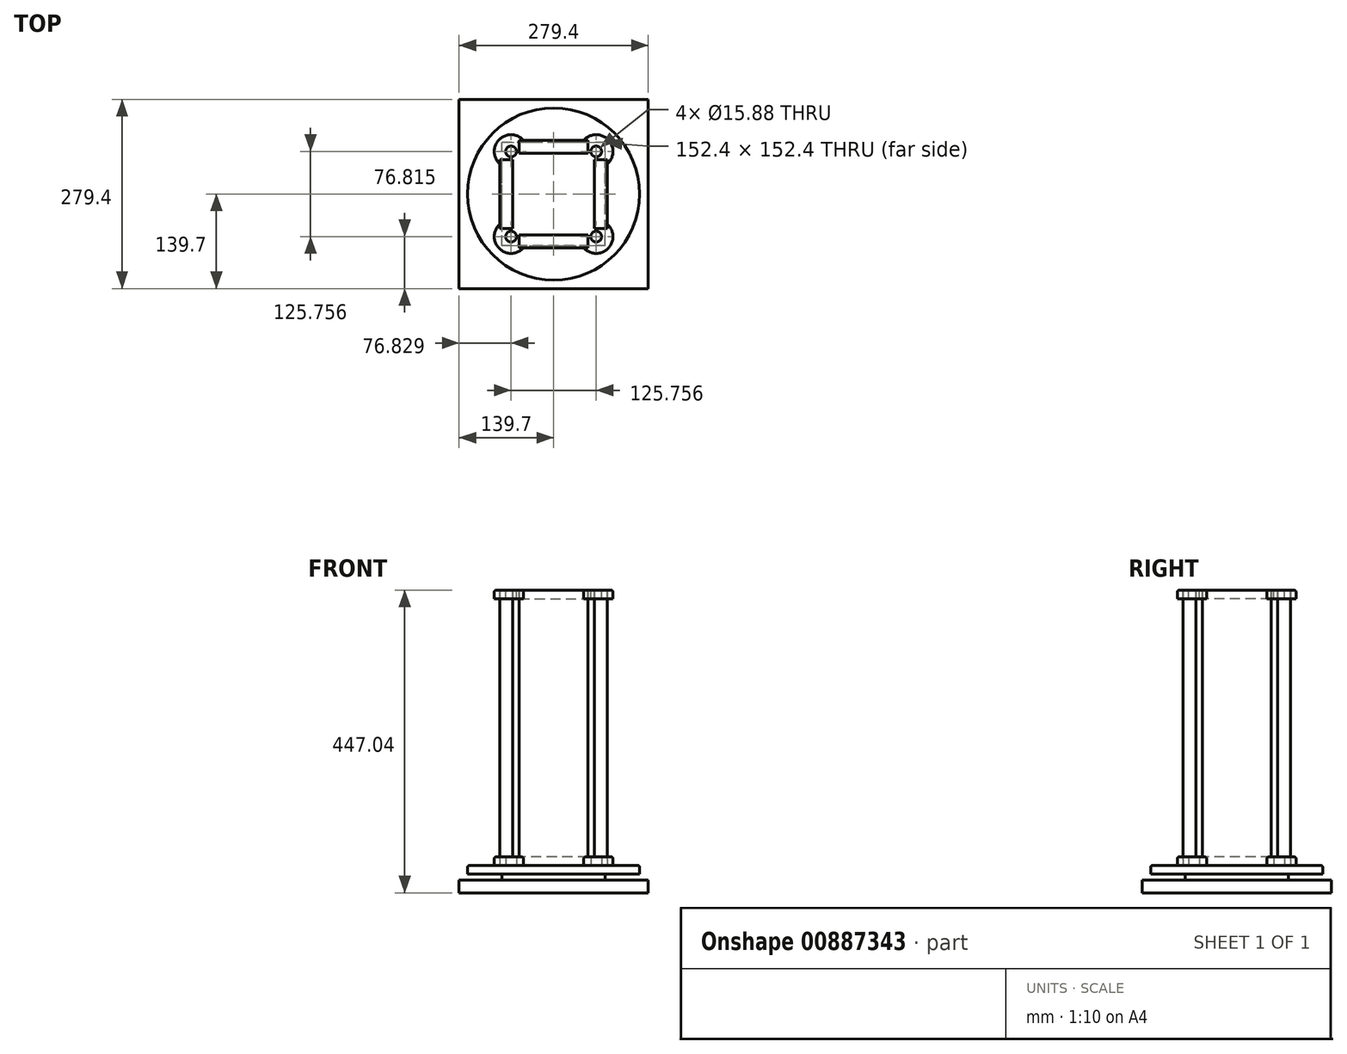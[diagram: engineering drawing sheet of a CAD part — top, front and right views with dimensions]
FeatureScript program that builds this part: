
annotation { "Feature Type Name" : "Feature", "Feature Type Description" : "" }
export const myFeature = defineFeature(function(context is Context, id is Id, definition is map)
    precondition{}
    {
        {
            var Q0;
            Q0=qCreatedBy(makeId("Top.planeOp"),FACE);
            var sketch = newSketch(context, id + "F0", { "sketchPlane" : qUnion([Q0])});
            skLineSegment(sketch, "E0.bottom", {"start": v(-139.7, 139.7) * mm, "end": v(139.7, 139.7) * mm});
            skLineSegment(sketch, "E0.top", {"start": v(-139.7, -139.7) * mm, "end": v(139.7, -139.7) * mm});
            skLineSegment(sketch, "E0.left", {"start": v(-139.7, 139.7) * mm, "end": v(-139.7, -139.7) * mm});
            skLineSegment(sketch, "E0.right", {"start": v(139.7, 139.7) * mm, "end": v(139.7, -139.7) * mm});
            skPoint(sketch, "E0.middle", {"position": v(0, 0) * mm});
            skSolve(sketch);
        }
        {
            var Q0;
            Q0=makeQuery(id+"F0.imprint","IMPRINT",FACE,{"disambiguationData":[TD([[makeQuery(id+"F0.imprint","IMPRINT",EDGE,{"derivedFrom":sQuery(id+"F0.wireOp",EDGE,"E0.bottom")}),-1.0]])]});
            extrude(context, id + "F1", {"entities" : qUnion([Q0]), "depth" : 19.05 * mm, "offsetDistance" : 25.4 * mm});
        }
        {
            var Q0;
            Q0=makeQuery(id+"F1.opExtrude","CAP_FACE",FACE,{"disambiguationData":[OSD([sQuery(id+"F0.wireOp",EDGE,"E0.bottom"),sQuery(id+"F0.wireOp",EDGE,"E0.top"),sQuery(id+"F0.wireOp",EDGE,"E0.left"),sQuery(id+"F0.wireOp",EDGE,"E0.right")])],"isStart":false});
            var sketch = newSketch(context, id + "F2", { "sketchPlane" : qUnion([Q0])});
            skLineSegment(sketch, "E1.bottom", {"start": v(76.2, -76.2) * mm, "end": v(-76.2, -76.2) * mm});
            skLineSegment(sketch, "E1.top", {"start": v(76.2, 76.2) * mm, "end": v(-76.2, 76.2) * mm});
            skLineSegment(sketch, "E1.left", {"start": v(76.2, -76.2) * mm, "end": v(76.2, 76.2) * mm});
            skLineSegment(sketch, "E1.right", {"start": v(-76.2, -76.2) * mm, "end": v(-76.2, 76.2) * mm});
            skPoint(sketch, "E1.middle", {"position": v(0, 0) * mm});
            skSolve(sketch);
        }
        {
            var Q0;
            Q0 = qSketchRegion(id + "F2", true);
            extrude(context, id + "F3", {"entities" : qUnion([Q0]), "operationType" : NewBodyOperationType.ADD, "depth" : 8.9 * mm, "offsetDistance" : 25.4 * mm});
        }
        {
            var Q0;
            Q0=qCreatedBy(makeId("Top.planeOp"),FACE);
            cPlane(context, id + "F4", {"entities" : qUnion([Q0]), "cplaneType" : CPlaneType.OFFSET, "offset" : 27.94 * mm, "width" : 152.4 * mm, "height" : 152.4 * mm});
        }
        {
            var Q0;
            Q0=qCreatedBy(id+"F4.planeOp",FACE);
            var sketch = newSketch(context, id + "F5", { "sketchPlane" : qUnion([Q0])});
            skCircle(sketch, "E2", {"center": v(0, 0) * mm, "radius": 127 * mm});
            skSolve(sketch);
        }
        {
            var Q0;
            Q0=makeQuery(id+"F5.imprint","IMPRINT",FACE,{"disambiguationData":[TD([[makeQuery(id+"F5.imprint","IMPRINT",EDGE,{"derivedFrom":sQuery(id+"F5.wireOp",EDGE,"E2")}),1.0]])]});
            extrude(context, id + "F6", {"entities" : qUnion([Q0]), "operationType" : NewBodyOperationType.ADD, "depth" : 12.7 * mm, "offsetDistance" : 25.4 * mm});
        }
        {
            var Q0;
            Q0=makeQuery(id+"F6.opExtrude","CAP_FACE",FACE,{"disambiguationData":[OSD([sQuery(id+"F5.wireOp",EDGE,"E2")])],"isStart":false});
            var sketch = newSketch(context, id + "F7", { "sketchPlane" : qUnion([Q0])});
            skLineSegment(sketch, "E3.bottom", {"start": v(50.8, -79.38) * mm, "end": v(-50.8, -79.38) * mm});
            skLineSegment(sketch, "E3.top", {"start": v(50.8, -60.33) * mm, "end": v(-50.8, -60.32) * mm});
            skLineSegment(sketch, "E3.left", {"start": v(50.8, -79.38) * mm, "end": v(50.8, -60.33) * mm});
            skLineSegment(sketch, "E3.right", {"start": v(-50.8, -79.38) * mm, "end": v(-50.8, -60.32) * mm});
            skPoint(sketch, "E3.middle", {"position": v(0, -69.85) * mm});
            skLineSegment(sketch, "E4.1.0", {"start": v(79.38, 50.8) * mm, "end": v(79.38, -50.8) * mm});
            skLineSegment(sketch, "E4.1.1", {"start": v(79.38, -50.8) * mm, "end": v(60.32, -50.8) * mm});
            skLineSegment(sketch, "E4.1.2", {"start": v(60.33, 50.8) * mm, "end": v(60.32, -50.8) * mm});
            skLineSegment(sketch, "E4.1.3", {"start": v(79.38, 50.8) * mm, "end": v(60.33, 50.8) * mm});
            skLineSegment(sketch, "E4.2.0", {"start": v(-50.8, 79.38) * mm, "end": v(50.8, 79.38) * mm});
            skLineSegment(sketch, "E4.2.1", {"start": v(50.8, 79.38) * mm, "end": v(50.8, 60.32) * mm});
            skLineSegment(sketch, "E4.2.2", {"start": v(-50.8, 60.33) * mm, "end": v(50.8, 60.32) * mm});
            skLineSegment(sketch, "E4.2.3", {"start": v(-50.8, 79.38) * mm, "end": v(-50.8, 60.33) * mm});
            skLineSegment(sketch, "E4.3.0", {"start": v(-79.38, -50.8) * mm, "end": v(-79.38, 50.8) * mm});
            skLineSegment(sketch, "E4.3.1", {"start": v(-79.38, 50.8) * mm, "end": v(-60.32, 50.8) * mm});
            skLineSegment(sketch, "E4.3.2", {"start": v(-60.33, -50.8) * mm, "end": v(-60.32, 50.8) * mm});
            skLineSegment(sketch, "E4.3.3", {"start": v(-79.38, -50.8) * mm, "end": v(-60.33, -50.8) * mm});
            skPoint(sketch, "E4.center", {"position": v(0, 0) * mm});
            skCircle(sketch, "E5", {"center": v(-62.87, -62.86) * mm, "radius": 7.94 * mm});
            skLineSegment(sketch, "E6", {"start": v(-62.87, -62.86) * mm, "end": v(0, 0) * mm, "construction": true});
            skLineSegment(sketch, "E7", {"start": v(0, 0) * mm, "end": v(0, -69.85) * mm, "construction": true});
            skLineSegment(sketch, "E8", {"start": v(-62.87, -62.86) * mm, "end": v(-50.8, -62.86) * mm, "construction": true});
            skLineSegment(sketch, "E9", {"start": v(-62.87, -62.86) * mm, "end": v(-62.87, -50.8) * mm, "construction": true});
            skCircle(sketch, "E10.1.0", {"center": v(62.86, -62.87) * mm, "radius": 7.94 * mm});
            skCircle(sketch, "E10.2.0", {"center": v(62.87, 62.86) * mm, "radius": 7.94 * mm});
            skCircle(sketch, "E10.3.0", {"center": v(-62.86, 62.87) * mm, "radius": 7.94 * mm});
            skSolve(sketch);
        }
        {
            var Q0;
            Q0=makeQuery(id+"F7.imprint","IMPRINT",FACE,{"disambiguationData":[TD([[makeQuery(id+"F7.imprint","IMPRINT",EDGE,{"derivedFrom":sQuery(id+"F7.wireOp",EDGE,"E3.bottom")}),-1.0]])]});
            var Q1;
            Q1=makeQuery(id+"F7.imprint","IMPRINT",FACE,{"disambiguationData":[TD([[makeQuery(id+"F7.imprint","IMPRINT",EDGE,{"derivedFrom":sQuery(id+"F7.wireOp",EDGE,"E4.3.0")}),-1.0]])]});
            var Q2;
            Q2=makeQuery(id+"F7.imprint","IMPRINT",FACE,{"disambiguationData":[TD([[makeQuery(id+"F7.imprint","IMPRINT",EDGE,{"derivedFrom":sQuery(id+"F7.wireOp",EDGE,"E4.2.0")}),-1.0]])]});
            var Q3;
            Q3=makeQuery(id+"F7.imprint","IMPRINT",FACE,{"disambiguationData":[TD([[makeQuery(id+"F7.imprint","IMPRINT",EDGE,{"derivedFrom":sQuery(id+"F7.wireOp",EDGE,"E4.1.0")}),-1.0]])]});
            extrude(context, id + "F8", {"entities" : qUnion([Q0, Q1, Q2, Q3]), "operationType" : NewBodyOperationType.ADD, "depth" : 406.4 * mm, "offsetDistance" : 25.4 * mm});
        }
        {
            var Q0;
            Q0=sQuery(id+"F7.wireOp",EDGE,"E10.3.0");
            var Q1;
            Q1=sQuery(id+"F7.wireOp",EDGE,"E10.2.0");
            var Q2;
            Q2=sQuery(id+"F7.wireOp",EDGE,"E10.1.0");
            var Q3;
            Q3=sQuery(id+"F7.wireOp",EDGE,"E5");
            extrude(context, id + "F9", {"bodyType" : ToolBodyType.SURFACE, "surfaceEntities" : qUnion([Q0, Q1, Q2, Q3]), "depth" : 406.4 * mm, "offsetDistance" : 25.4 * mm});
        }
        {
            var Q0;
            Q0=qCreatedBy(makeId("Front.planeOp"),FACE);
            cPlane(context, id + "F10", {"entities" : qUnion([Q0]), "cplaneType" : CPlaneType.OFFSET, "offset" : 50.8 * mm, "width" : 152.4 * mm, "height" : 152.4 * mm});
        }
        {
            var Q0;
            Q0=qCreatedBy(id+"F10.planeOp",FACE);
            var sketch = newSketch(context, id + "F11", { "sketchPlane" : qUnion([Q0])});
            skLineSegment(sketch, "E11", {"start": v(0, 0) * mm, "end": v(-62.87, 0) * mm, "construction": true});
            skLineSegment(sketch, "E12", {"start": v(-62.87, 0) * mm, "end": v(-62.87, 457.2) * mm, "construction": true});
            skLineSegment(sketch, "E13", {"start": v(0, 0) * mm, "end": v(0, 518.12) * mm, "construction": true});
            skCircle(sketch, "E14", {"center": v(-62.87, 457.2) * mm, "radius": 7.94 * mm});
            skCircle(sketch, "E15.MirrorC", {"center": v(62.87, 457.2) * mm, "radius": 7.94 * mm});
            skSolve(sketch);
        }
        {
            var Q0;
            Q0=sQuery(id+"F11.wireOp",EDGE,"E14");
            var Q1;
            Q1=sQuery(id+"F11.wireOp",EDGE,"E15.MirrorC");
            extrude(context, id + "F12", {"bodyType" : ToolBodyType.SURFACE, "surfaceEntities" : qUnion([Q0, Q1]), "oppositeDirection" : true, "depth" : 101.6 * mm, "offsetDistance" : 25.4 * mm});
        }
        {
            var Q0;
            Q0=qCreatedBy(makeId("Right.planeOp"),FACE);
            cPlane(context, id + "F13", {"entities" : qUnion([Q0]), "cplaneType" : CPlaneType.OFFSET, "offset" : 50.8 * mm, "width" : 152.4 * mm, "height" : 152.4 * mm});
        }
        {
            var Q0;
            Q0=qCreatedBy(id+"F13.planeOp",FACE);
            var sketch = newSketch(context, id + "F14", { "sketchPlane" : qUnion([Q0])});
            skLineSegment(sketch, "E16", {"start": v(0, 0) * mm, "end": v(62.87, 0) * mm, "construction": true});
            skLineSegment(sketch, "E17", {"start": v(62.87, 0) * mm, "end": v(62.87, 457.2) * mm, "construction": true});
            skLineSegment(sketch, "E18", {"start": v(0, 0) * mm, "end": v(0, 512.3) * mm, "construction": true});
            skCircle(sketch, "E19", {"center": v(62.86, 457.2) * mm, "radius": 7.94 * mm});
            skCircle(sketch, "E20.MirrorC", {"center": v(-62.86, 457.2) * mm, "radius": 7.94 * mm});
            skSolve(sketch);
        }
        {
            var Q0;
            Q0=sQuery(id+"F14.wireOp",EDGE,"E20.MirrorC");
            var Q1;
            Q1=sQuery(id+"F14.wireOp",EDGE,"E19");
            extrude(context, id + "F15", {"bodyType" : ToolBodyType.SURFACE, "surfaceEntities" : qUnion([Q0, Q1]), "oppositeDirection" : true, "depth" : 101.6 * mm, "offsetDistance" : 25.4 * mm});
        }
        {
            var Q0;
            Q0=makeQuery(id+"F12.opExtrude","CAP_EDGE",EDGE,{"disambiguationData":[OSD([sQuery(id+"F11.wireOp",EDGE,"E15.MirrorC")])],"isStart":false});
            var Q1;
            Q1=makeQuery(id+"F12.opExtrude","CAP_EDGE",EDGE,{"disambiguationData":[OSD([sQuery(id+"F11.wireOp",EDGE,"E14")])],"isStart":false});
            var Q2;
            Q2=makeQuery(id+"F8.opExtrude","CAP_EDGE",EDGE,{"disambiguationData":[OSD([sQuery(id+"F7.wireOp",EDGE,"E4.1.3")])],"isStart":false});
            revolve(context, id + "F16", {"bodyType" : ToolBodyType.SURFACE, "surfaceOperationType" : NewSurfaceOperationType.ADD, "surfaceEntities" : qUnion([Q0, Q1]), "axis" : qUnion([Q2]), "revolveType" : RevolveType.ONE_DIRECTION, "angle" : 90 * degree});
        }
        {
            var Q0;
            Q0=makeQuery(id+"F15.opExtrude","CAP_EDGE",EDGE,{"disambiguationData":[OSD([sQuery(id+"F14.wireOp",EDGE,"E19")])],"isStart":true});
            var Q1;
            Q1=makeQuery(id+"F15.opExtrude","CAP_EDGE",EDGE,{"disambiguationData":[OSD([sQuery(id+"F14.wireOp",EDGE,"E20.MirrorC")])],"isStart":true});
            var Q2;
            Q2=makeQuery(id+"F8.opExtrude","CAP_EDGE",EDGE,{"disambiguationData":[OSD([sQuery(id+"F7.wireOp",EDGE,"E4.2.1")])],"isStart":false});
            revolve(context, id + "F17", {"bodyType" : ToolBodyType.SURFACE, "surfaceOperationType" : NewSurfaceOperationType.ADD, "surfaceEntities" : qUnion([Q0, Q1]), "axis" : qUnion([Q2]), "revolveType" : RevolveType.ONE_DIRECTION, "oppositeDirection" : true, "angle" : 90 * degree});
        }
        {
            var Q0;
            Q0=makeQuery(id+"F12.opExtrude","CAP_EDGE",EDGE,{"disambiguationData":[OSD([sQuery(id+"F11.wireOp",EDGE,"E15.MirrorC")])],"isStart":true});
            var Q1;
            Q1=makeQuery(id+"F12.opExtrude","CAP_EDGE",EDGE,{"disambiguationData":[OSD([sQuery(id+"F11.wireOp",EDGE,"E14")])],"isStart":true});
            var Q2;
            Q2=makeQuery(id+"F8.opExtrude","CAP_EDGE",EDGE,{"disambiguationData":[OSD([sQuery(id+"F7.wireOp",EDGE,"E4.3.3")])],"isStart":false});
            revolve(context, id + "F18", {"bodyType" : ToolBodyType.SURFACE, "surfaceOperationType" : NewSurfaceOperationType.ADD, "surfaceEntities" : qUnion([Q0, Q1]), "axis" : qUnion([Q2]), "revolveType" : RevolveType.ONE_DIRECTION, "angle" : 90 * degree});
        }
        {
            var Q0;
            Q0=makeQuery(id+"F15.opExtrude","CAP_EDGE",EDGE,{"disambiguationData":[OSD([sQuery(id+"F14.wireOp",EDGE,"E19")])],"isStart":false});
            var Q1;
            Q1=makeQuery(id+"F15.opExtrude","CAP_EDGE",EDGE,{"disambiguationData":[OSD([sQuery(id+"F14.wireOp",EDGE,"E20.MirrorC")])],"isStart":false});
            var Q2;
            Q2=makeQuery(id+"F8.opExtrude","CAP_EDGE",EDGE,{"disambiguationData":[OSD([sQuery(id+"F7.wireOp",EDGE,"E4.2.3")])],"isStart":false});
            revolve(context, id + "F19", {"bodyType" : ToolBodyType.SURFACE, "surfaceOperationType" : NewSurfaceOperationType.ADD, "surfaceEntities" : qUnion([Q0, Q1]), "axis" : qUnion([Q2]), "revolveType" : RevolveType.ONE_DIRECTION, "angle" : 90 * degree});
        }
        {
            var Q0;
            Q0=makeQuery(id+"F7.imprint","IMPRINT",FACE,{"disambiguationData":[TD([[makeQuery(id+"F7.imprint","IMPRINT",EDGE,{"derivedFrom":sQuery(id+"F7.wireOp",EDGE,"E3.bottom")}),1.0]])]});
            var sketch = newSketch(context, id + "F20", { "sketchPlane" : qUnion([Q0])});
            skLineSegment(sketch, "E21", {"start": v(0, -60.33) * mm, "end": v(50.8, -60.33) * mm});
            skLineSegment(sketch, "E22", {"start": v(50.8, -60.33) * mm, "end": v(50.8, -79.38) * mm});
            skLineSegment(sketch, "E23", {"start": v(50.8, -79.38) * mm, "end": v(44.45, -79.38) * mm});
            skLineSegment(sketch, "E24", {"start": v(60.32, 0) * mm, "end": v(60.32, -50.8) * mm});
            skLineSegment(sketch, "E25", {"start": v(60.32, -50.8) * mm, "end": v(79.38, -50.8) * mm});
            skLineSegment(sketch, "E26", {"start": v(79.38, -50.8) * mm, "end": v(79.38, -44.45) * mm});
            skArc(sketch, "E27", {"start": v(44.45, -79.38) * mm, "mid": v(80.35, -80.35) * mm, "end": v(79.38, -44.45) * mm});
            skCircle(sketch, "E28", {"center": v(62.86, -62.86) * mm, "radius": 7.94 * mm});
            skPoint(sketch, "E29.center", {"position": v(0, 0) * mm});
            skLineSegment(sketch, "E30", {"start": v(0, 0) * mm, "end": v(0, -60.33) * mm, "construction": true});
            skLineSegment(sketch, "E31", {"start": v(0, 0) * mm, "end": v(60.32, 0) * mm, "construction": true});
            skLineSegment(sketch, "E32", {"start": v(62.86, -62.86) * mm, "end": v(62.86, -50.8) * mm, "construction": true});
            skLineSegment(sketch, "E33", {"start": v(62.86, -62.86) * mm, "end": v(50.8, -62.86) * mm, "construction": true});
            skLineSegment(sketch, "E34", {"start": v(0, 0) * mm, "end": v(62.86, -62.86) * mm, "construction": true});
            skLineSegment(sketch, "E35.1.0", {"start": v(0, 60.32) * mm, "end": v(50.8, 60.32) * mm});
            skLineSegment(sketch, "E35.1.1", {"start": v(50.8, 60.32) * mm, "end": v(50.8, 79.38) * mm});
            skLineSegment(sketch, "E35.1.2", {"start": v(50.8, 79.38) * mm, "end": v(44.45, 79.38) * mm});
            skArc(sketch, "E35.1.3", {"start": v(79.38, 44.45) * mm, "mid": v(80.35, 80.35) * mm, "end": v(44.45, 79.38) * mm});
            skCircle(sketch, "E35.1.4", {"center": v(62.86, 62.86) * mm, "radius": 7.94 * mm});
            skLineSegment(sketch, "E35.1.5", {"start": v(60.33, 50.8) * mm, "end": v(79.38, 50.8) * mm});
            skLineSegment(sketch, "E35.1.6", {"start": v(60.33, 0) * mm, "end": v(60.33, 50.8) * mm});
            skLineSegment(sketch, "E35.1.7", {"start": v(79.38, 50.8) * mm, "end": v(79.38, 44.45) * mm});
            skLineSegment(sketch, "E35.2.0", {"start": v(-60.32, 0) * mm, "end": v(-60.32, 50.8) * mm});
            skLineSegment(sketch, "E35.2.1", {"start": v(-60.32, 50.8) * mm, "end": v(-79.38, 50.8) * mm});
            skLineSegment(sketch, "E35.2.2", {"start": v(-79.38, 50.8) * mm, "end": v(-79.38, 44.45) * mm});
            skArc(sketch, "E35.2.3", {"start": v(-44.45, 79.38) * mm, "mid": v(-80.35, 80.35) * mm, "end": v(-79.37, 44.45) * mm});
            skCircle(sketch, "E35.2.4", {"center": v(-62.86, 62.86) * mm, "radius": 7.94 * mm});
            skLineSegment(sketch, "E35.2.5", {"start": v(-50.8, 60.33) * mm, "end": v(-50.8, 79.38) * mm});
            skLineSegment(sketch, "E35.2.6", {"start": v(0, 60.33) * mm, "end": v(-50.8, 60.33) * mm});
            skLineSegment(sketch, "E35.2.7", {"start": v(-50.8, 79.38) * mm, "end": v(-44.45, 79.38) * mm});
            skLineSegment(sketch, "E35.3.0", {"start": v(0, -60.32) * mm, "end": v(-50.8, -60.32) * mm});
            skLineSegment(sketch, "E35.3.1", {"start": v(-50.8, -60.32) * mm, "end": v(-50.8, -79.37) * mm});
            skLineSegment(sketch, "E35.3.2", {"start": v(-50.8, -79.37) * mm, "end": v(-44.45, -79.37) * mm});
            skArc(sketch, "E35.3.3", {"start": v(-79.38, -44.45) * mm, "mid": v(-80.35, -80.35) * mm, "end": v(-44.45, -79.37) * mm});
            skCircle(sketch, "E35.3.4", {"center": v(-62.86, -62.86) * mm, "radius": 7.94 * mm});
            skLineSegment(sketch, "E35.3.5", {"start": v(-60.33, -50.8) * mm, "end": v(-79.38, -50.8) * mm});
            skLineSegment(sketch, "E35.3.6", {"start": v(-60.33, 0) * mm, "end": v(-60.33, -50.8) * mm});
            skLineSegment(sketch, "E35.3.7", {"start": v(-79.38, -50.8) * mm, "end": v(-79.38, -44.45) * mm});
            skSolve(sketch);
        }
        {
            var Q0;
            Q0=makeQuery(id+"F20.imprint","IMPRINT",FACE,{"disambiguationData":[TD([[makeQuery(id+"F20.imprint","IMPRINT",EDGE,{"derivedFrom":sQuery(id+"F20.wireOp",EDGE,"E21")}),-1.0]])]});
            extrude(context, id + "F21", {"entities" : qUnion([Q0]), "operationType" : NewBodyOperationType.ADD, "depth" : 12.7 * mm, "offsetDistance" : 25.4 * mm});
        }
        {
            var Q0;
            Q0=makeQuery(id+"F21.opExtrude","CAP_EDGE",EDGE,{"disambiguationData":[OSD([sQuery(id+"F20.wireOp",EDGE,"E35.3.3")])],"isStart":false});
            var Q1;
            Q1=makeQuery(id+"F21.opExtrude","CAP_EDGE",EDGE,{"disambiguationData":[OSD([sQuery(id+"F20.wireOp",EDGE,"E27")])],"isStart":false});
            var Q2;
            Q2=makeQuery(id+"F21.opExtrude","CAP_EDGE",EDGE,{"disambiguationData":[OSD([sQuery(id+"F20.wireOp",EDGE,"E35.1.3")])],"isStart":false});
            var Q3;
            Q3=makeQuery(id+"F21.opExtrude","CAP_EDGE",EDGE,{"disambiguationData":[OSD([sQuery(id+"F20.wireOp",EDGE,"E35.2.3")])],"isStart":false});
            fillet(context, id + "F22", {"entities" : qUnion([Q0, Q1, Q2, Q3]), "radius" : 3.17 * mm, "tangentPropagation" : true, "allowEdgeOverflow" : false});
        }
        {
            var Q0;
            {var subQ0=sQuery(id+"F5.wireOp",EDGE,"E2");Q0=makeQuery(id+"F21.boolean.opBoolean","SPLIT",FACE,{"disambiguationData":[TD([makeQuery(id+"F6.opExtrude","SWEPT_FACE",FACE,{"disambiguationData":[OSD([subQ0])]})])],"derivedFrom":makeQuery(id+"F6.opExtrude","CAP_FACE",FACE,{"disambiguationData":[OSD([subQ0])],"isStart":false})});}
            cPlane(context, id + "F23", {"entities" : qUnion([Q0]), "cplaneType" : CPlaneType.OFFSET, "offset" : 406.4 * mm, "width" : 152.4 * mm, "height" : 152.4 * mm});
        }
        {
            var Q0;
            Q0=qCreatedBy(id+"F23.planeOp",FACE);
            var sketch = newSketch(context, id + "F24", { "sketchPlane" : qUnion([Q0])});
            skLineSegment(sketch, "E36", {"start": v(0, 0) * mm, "end": v(0, -60.3) * mm, "construction": true});
            skLineSegment(sketch, "E37", {"start": v(0, 0) * mm, "end": v(60.3, 0) * mm, "construction": true});
            skLineSegment(sketch, "E38", {"start": v(60.3, 0) * mm, "end": v(60.3, -50.83) * mm});
            skLineSegment(sketch, "E39", {"start": v(60.3, -50.83) * mm, "end": v(79.4, -50.83) * mm});
            skLineSegment(sketch, "E40", {"start": v(79.4, -50.83) * mm, "end": v(79.4, -44.48) * mm});
            skLineSegment(sketch, "E41", {"start": v(0, -60.3) * mm, "end": v(50.83, -60.3) * mm});
            skLineSegment(sketch, "E42", {"start": v(50.83, -60.3) * mm, "end": v(50.83, -79.4) * mm});
            skLineSegment(sketch, "E43", {"start": v(50.83, -79.4) * mm, "end": v(44.48, -79.4) * mm});
            skArc(sketch, "E44", {"start": v(44.48, -79.4) * mm, "mid": v(80.37, -80.37) * mm, "end": v(79.4, -44.48) * mm});
            skCircle(sketch, "E45", {"center": v(62.88, -62.88) * mm, "radius": 7.94 * mm});
            skLineSegment(sketch, "E46.1.0", {"start": v(60.3, -0.01) * mm, "end": v(60.3, 50.81) * mm});
            skLineSegment(sketch, "E46.1.1", {"start": v(60.3, 50.81) * mm, "end": v(79.4, 50.81) * mm});
            skLineSegment(sketch, "E46.1.2", {"start": v(79.4, 50.81) * mm, "end": v(79.4, 44.46) * mm});
            skArc(sketch, "E46.1.3", {"start": v(79.4, 44.46) * mm, "mid": v(80.37, 80.36) * mm, "end": v(44.48, 79.39) * mm});
            skLineSegment(sketch, "E46.1.4", {"start": v(50.83, 79.39) * mm, "end": v(44.48, 79.39) * mm});
            skLineSegment(sketch, "E46.1.5", {"start": v(50.83, 60.29) * mm, "end": v(50.83, 79.39) * mm});
            skLineSegment(sketch, "E46.1.6", {"start": v(0, 60.29) * mm, "end": v(50.83, 60.29) * mm});
            skCircle(sketch, "E46.1.7", {"center": v(62.88, 62.87) * mm, "radius": 7.94 * mm});
            skLineSegment(sketch, "E46.2.0", {"start": v(0.01, 60.29) * mm, "end": v(-50.81, 60.29) * mm});
            skLineSegment(sketch, "E46.2.1", {"start": v(-50.81, 60.29) * mm, "end": v(-50.81, 79.39) * mm});
            skLineSegment(sketch, "E46.2.2", {"start": v(-50.81, 79.39) * mm, "end": v(-44.46, 79.39) * mm});
            skArc(sketch, "E46.2.3", {"start": v(-44.46, 79.39) * mm, "mid": v(-80.36, 80.36) * mm, "end": v(-79.39, 44.46) * mm});
            skLineSegment(sketch, "E46.2.4", {"start": v(-79.39, 50.81) * mm, "end": v(-79.39, 44.46) * mm});
            skLineSegment(sketch, "E46.2.5", {"start": v(-60.29, 50.81) * mm, "end": v(-79.39, 50.81) * mm});
            skLineSegment(sketch, "E46.2.6", {"start": v(-60.29, -0.01) * mm, "end": v(-60.29, 50.81) * mm});
            skCircle(sketch, "E46.2.7", {"center": v(-62.87, 62.87) * mm, "radius": 7.94 * mm});
            skLineSegment(sketch, "E46.3.0", {"start": v(-60.29, 0) * mm, "end": v(-60.29, -50.83) * mm});
            skLineSegment(sketch, "E46.3.1", {"start": v(-60.29, -50.83) * mm, "end": v(-79.39, -50.83) * mm});
            skLineSegment(sketch, "E46.3.2", {"start": v(-79.39, -50.83) * mm, "end": v(-79.39, -44.48) * mm});
            skArc(sketch, "E46.3.3", {"start": v(-79.39, -44.48) * mm, "mid": v(-80.36, -80.37) * mm, "end": v(-44.46, -79.4) * mm});
            skLineSegment(sketch, "E46.3.4", {"start": v(-50.81, -79.4) * mm, "end": v(-44.46, -79.4) * mm});
            skLineSegment(sketch, "E46.3.5", {"start": v(-50.81, -60.3) * mm, "end": v(-50.81, -79.4) * mm});
            skLineSegment(sketch, "E46.3.6", {"start": v(0.01, -60.3) * mm, "end": v(-50.81, -60.3) * mm});
            skCircle(sketch, "E46.3.7", {"center": v(-62.87, -62.88) * mm, "radius": 7.94 * mm});
            skPoint(sketch, "E46.center", {"position": v(0, 0) * mm});
            skSolve(sketch);
        }
        {
            var Q0;
            Q0=makeQuery(id+"F24.imprint","IMPRINT",FACE,{"disambiguationData":[TD([[makeQuery(id+"F24.imprint","IMPRINT",EDGE,{"derivedFrom":sQuery(id+"F24.wireOp",EDGE,"E38")}),-1.0]])]});
            extrude(context, id + "F25", {"entities" : qUnion([Q0]), "operationType" : NewBodyOperationType.ADD, "oppositeDirection" : true, "depth" : 12.7 * mm, "offsetDistance" : 25.4 * mm});
        }
        {
            var Q0;
            Q0=makeQuery(id+"F25.opExtrude","CAP_EDGE",EDGE,{"disambiguationData":[OSD([sQuery(id+"F24.wireOp",EDGE,"E46.3.3")])],"isStart":true});
            var Q1;
            Q1=makeQuery(id+"F25.opExtrude","CAP_EDGE",EDGE,{"disambiguationData":[OSD([sQuery(id+"F24.wireOp",EDGE,"E44")])],"isStart":true});
            var Q2;
            Q2=makeQuery(id+"F25.opExtrude","CAP_EDGE",EDGE,{"disambiguationData":[OSD([sQuery(id+"F24.wireOp",EDGE,"E46.1.3")])],"isStart":true});
            var Q3;
            Q3=makeQuery(id+"F25.opExtrude","CAP_EDGE",EDGE,{"disambiguationData":[OSD([sQuery(id+"F24.wireOp",EDGE,"E46.2.3")])],"isStart":true});
            fillet(context, id + "F26", {"entities" : qUnion([Q0, Q1, Q2, Q3]), "radius" : 3.17 * mm, "tangentPropagation" : true, "allowEdgeOverflow" : false});
        }
        {
            var Q0;
            Q0=makeQuery(id+"F6.opExtrude","CAP_EDGE",EDGE,{"disambiguationData":[OSD([sQuery(id+"F5.wireOp",EDGE,"E2")])],"isStart":false});
            fillet(context, id + "F27", {"entities" : qUnion([Q0]), "radius" : 3.17 * mm, "tangentPropagation" : true, "allowEdgeOverflow" : false});
        }
    });
